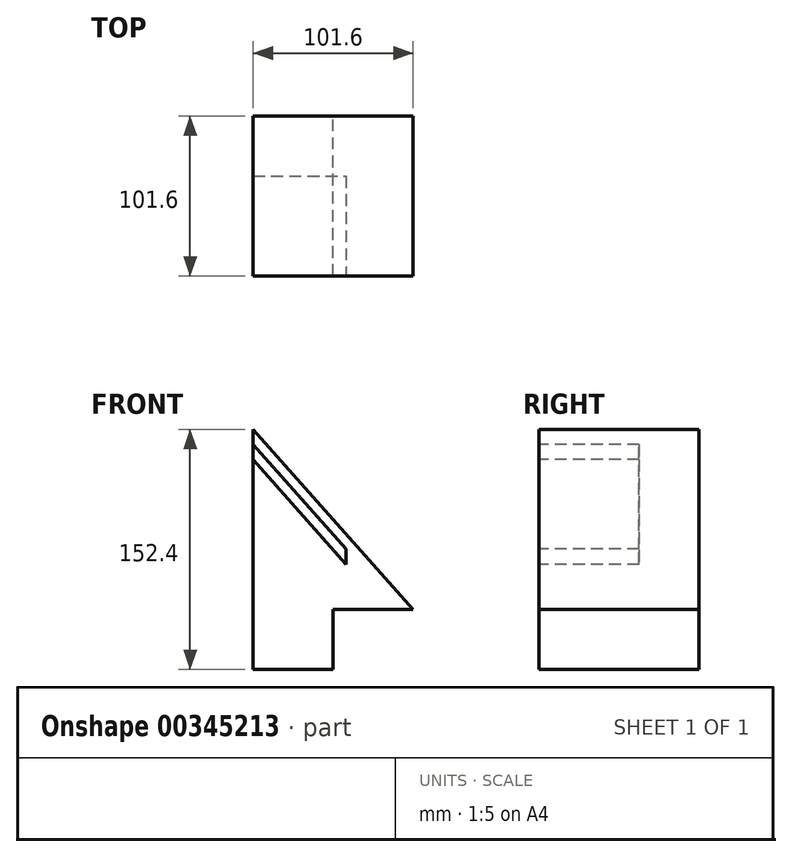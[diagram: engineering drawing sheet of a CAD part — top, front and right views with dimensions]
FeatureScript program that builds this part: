
annotation { "Feature Type Name" : "Feature", "Feature Type Description" : "" }
export const myFeature = defineFeature(function(context is Context, id is Id, definition is map)
    precondition{}
    {
        {
            var Q0;
            Q0=qCreatedBy(makeId("Front.planeOp"),FACE);
            var sketch = newSketch(context, id + "F0", { "sketchPlane" : qUnion([Q0])});
            skLineSegment(sketch, "E0.top", {"start": v(-61.33, -55.16) * mm, "end": v(-10.53, -55.16) * mm});
            skPoint(sketch, "E0.middle", {"position": v(-10.53, -36.1) * mm});
            skLineSegment(sketch, "E1", {"start": v(-10.53, -55.16) * mm, "end": v(-10.53, -17.06) * mm});
            skLineSegment(sketch, "E2", {"start": v(-10.53, -17.06) * mm, "end": v(40.27, -17.06) * mm});
            skLineSegment(sketch, "E3", {"start": v(40.27, -17.06) * mm, "end": v(-61.33, 97.24) * mm});
            skPoint(sketch, "E4.orphan", {"position": v(40.27, -55.16) * mm});
            skLineSegment(sketch, "E5", {"start": v(40.27, -17.06) * mm, "end": v(40.27, -17.06) * mm});
            skPoint(sketch, "E6.start.orphan", {"position": v(-61.33, -17.06) * mm});
            skLineSegment(sketch, "E7", {"start": v(-61.33, 97.24) * mm, "end": v(-61.33, -55.16) * mm});
            skSolve(sketch);
        }
        {
            var Q0;
            Q0=makeQuery(id+"F0.imprint","IMPRINT",FACE,{"disambiguationData":[TD([[makeQuery(id+"F0.imprint","IMPRINT",EDGE,{"derivedFrom":sQuery(id+"F0.wireOp",EDGE,"E0.top")}),1.0]])]});
            extrude(context, id + "F1", {"entities" : qUnion([Q0]), "depth" : 101.6 * mm});
        }
        {
            var Q0;
            Q0=makeQuery(id+"F1.opExtrude","CAP_FACE",FACE,{"disambiguationData":[OSD([sQuery(id+"F0.wireOp",EDGE,"E0.top"),sQuery(id+"F0.wireOp",EDGE,"E1"),sQuery(id+"F0.wireOp",EDGE,"E2"),sQuery(id+"F0.wireOp",EDGE,"E3"),sQuery(id+"F0.wireOp",EDGE,"E5"),sQuery(id+"F0.wireOp",EDGE,"E7")])],"isStart":false});
            var sketch = newSketch(context, id + "F2", { "sketchPlane" : qUnion([Q0])});
            skLineSegment(sketch, "E8", {"start": v(-61.33, 78.13) * mm, "end": v(-2.27, 11.68) * mm});
            skLineSegment(sketch, "E9", {"start": v(-2.27, 11.68) * mm, "end": v(-2.27, 21.24) * mm});
            skLineSegment(sketch, "E10", {"start": v(-2.27, 21.24) * mm, "end": v(-61.33, 87.68) * mm});
            skSolve(sketch);
        }
        {
            var Q0;
            {var subQ0=sQuery(id+"F2.wireOp",EDGE,"E8");Q0=makeQuery(id+"F2.imprint","IMPRINT",FACE,{"disambiguationData":[TD([[makeQuery(id+"F2.imprint","IMPRINT",EDGE,{"derivedFrom":subQ0}),1.0]])]});}
            extrude(context, id + "F3", {"entities" : qUnion([Q0]), "operationType" : NewBodyOperationType.REMOVE, "oppositeDirection" : true, "depth" : 63.5 * mm});
        }
    });
